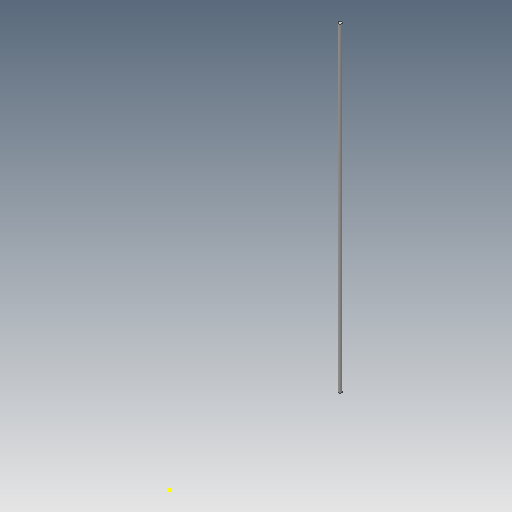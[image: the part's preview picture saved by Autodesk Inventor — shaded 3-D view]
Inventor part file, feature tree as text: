
AUTODESK INVENTOR PART (.ipt)
format: ipt  version: 2017 (Build 210142000, 142)  size: 75,264 bytes
history: native  units: mm
features: other x3, sketch x2
ambient origin geometry x8: Origin, YZ Plane, XZ Plane, XY Plane, X Axis, Y Axis, Z Axis, Center Point
bodies: Solid1 (feature_tree)
feature tree (5):
  other  "Lead Screw-A_CPY.ipt"
  other  "Solid1::Lead Screw-A_CPY.ipt"
  other  "TaggingFeature1"
  sketch  "Sketch1"  dims[d0=10.0mm]
  sketch  "Sketch2"
